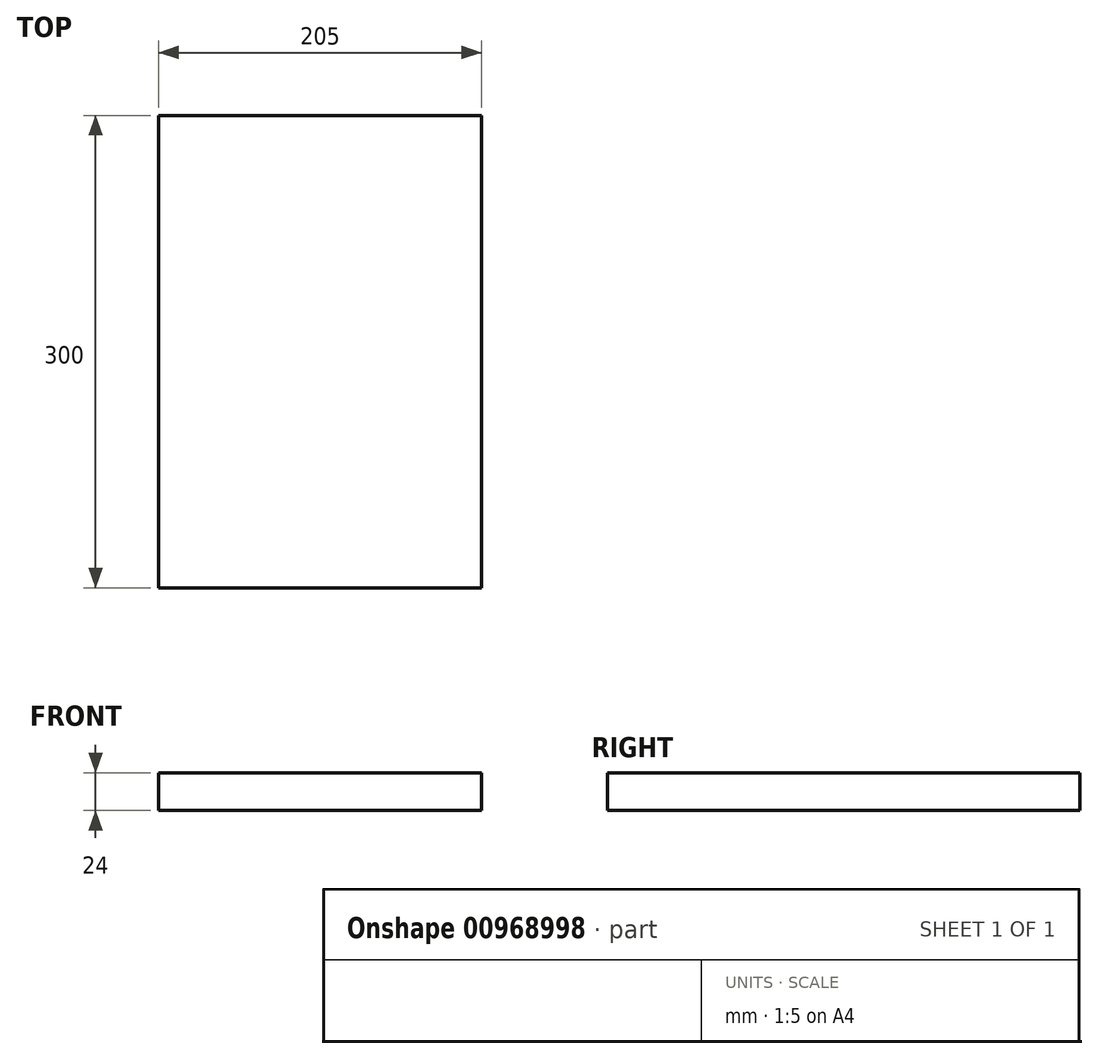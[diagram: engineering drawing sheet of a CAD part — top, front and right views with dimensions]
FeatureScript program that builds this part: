
annotation { "Feature Type Name" : "Feature", "Feature Type Description" : "" }
export const myFeature = defineFeature(function(context is Context, id is Id, definition is map)
    precondition{}
    {
        {
            var Q0;
            Q0=qCreatedBy(makeId("Top.planeOp"),FACE);
            var sketch = newSketch(context, id + "F0", { "sketchPlane" : qUnion([Q0])});
            skLineSegment(sketch, "E0.bottom", {"start": v(102.5, 150) * mm, "end": v(-102.5, 150) * mm});
            skLineSegment(sketch, "E0.top", {"start": v(102.5, -150) * mm, "end": v(-102.5, -150) * mm});
            skLineSegment(sketch, "E0.left", {"start": v(102.5, 150) * mm, "end": v(102.5, -150) * mm});
            skLineSegment(sketch, "E0.right", {"start": v(-102.5, 150) * mm, "end": v(-102.5, -150) * mm});
            skPoint(sketch, "E0.middle", {"position": v(0, 0) * mm});
            skSolve(sketch);
        }
        {
            var Q0;
            Q0=makeQuery(id+"F0.imprint","IMPRINT",FACE,{"disambiguationData":[TD([[makeQuery(id+"F0.imprint","IMPRINT",EDGE,{"derivedFrom":sQuery(id+"F0.wireOp",EDGE,"E0.bottom")}),1.0]])]});
            extrude(context, id + "F1", {"entities" : qUnion([Q0]), "depth" : 24 * mm, "offsetDistance" : 25 * mm});
        }
    });
